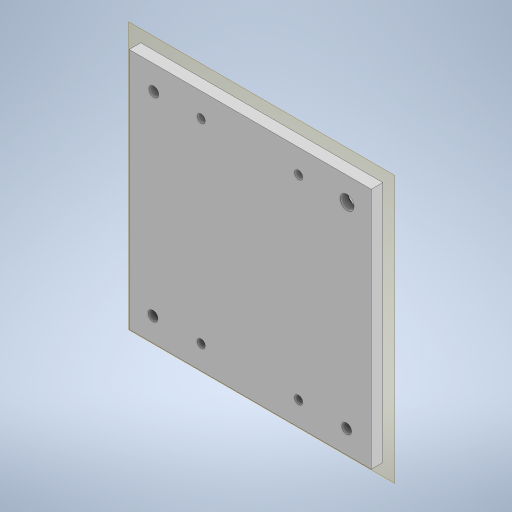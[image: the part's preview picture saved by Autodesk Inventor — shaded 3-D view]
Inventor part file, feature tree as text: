
AUTODESK INVENTOR PART (.ipt)
format: ipt  version: 2023.2 (Build 272271000, 271)  size: 560,640 bytes
history: native  units: mm
features: reference x16, sketch x4, hole x3, other x3, plane x1, extrude x1
ambient origin geometry x8: Origin, YZ Plane, XZ Plane, XY Plane, X Axis, Y Axis, Z Axis, Center Point
bodies: Solid1 (feature_tree)
feature tree (28):
  plane  "Work Plane1"
  extrude  "Extrusion1"  [1 undecoded]
  hole  "Hole1"  [1 undecoded]
  hole  "Hole2"  [1 undecoded]
  hole  "Hole3"  [1 undecoded]
  sketch  "Sketch3"  dims[d8=6.0mm d9=0.0mm]
  reference  "Reference15"
  reference  "Reference16"
  reference  "Reference17"
  reference  "Reference18"
  reference  "Reference19"
  reference  "Reference20"
  reference  "Reference21"
  reference  "Reference22"
  reference  "Reference23"
  reference  "Reference24"
  reference  "Reference25"
  reference  "Reference26"
  reference  "Reference27"
  reference  "Reference28"
  reference  "Reference29"
  reference  "Reference30"
  sketch  "Sketch4"  dims[d10=7.2mm d11=6.0mm d12=12.25mm d13=2.0mm d14=90.0deg d15=8.0mm d16=20.594885mm]
  sketch  "Sketch5"  dims[d17=5.1mm d18=6.0mm d19=9.2mm d20=2.0mm d21=90.0deg d22=8.0mm d23=20.594885mm]
  sketch  "Sketch6"  dims[d24=4.2mm d25=6.0mm d26=9.2mm d27=2.0mm d28=90.0deg d29=8.0mm d30=20.594885mm]
  parser-record x1  (decoder bookkeeping rows leaked as tree rows — omitted from the tree; the rows remain in map.json)
  other  "Main Assembly.iam"
  other  "Z axis carriage small:1"
note: 4 required parameter values undecoded (feature->parameter linkage not recoverable at this tier; creation-order binding heuristic only, values carry confidence <= 0.55)
note: 1 file-system path scrubbed to <path> (originals preserved in map.json)
